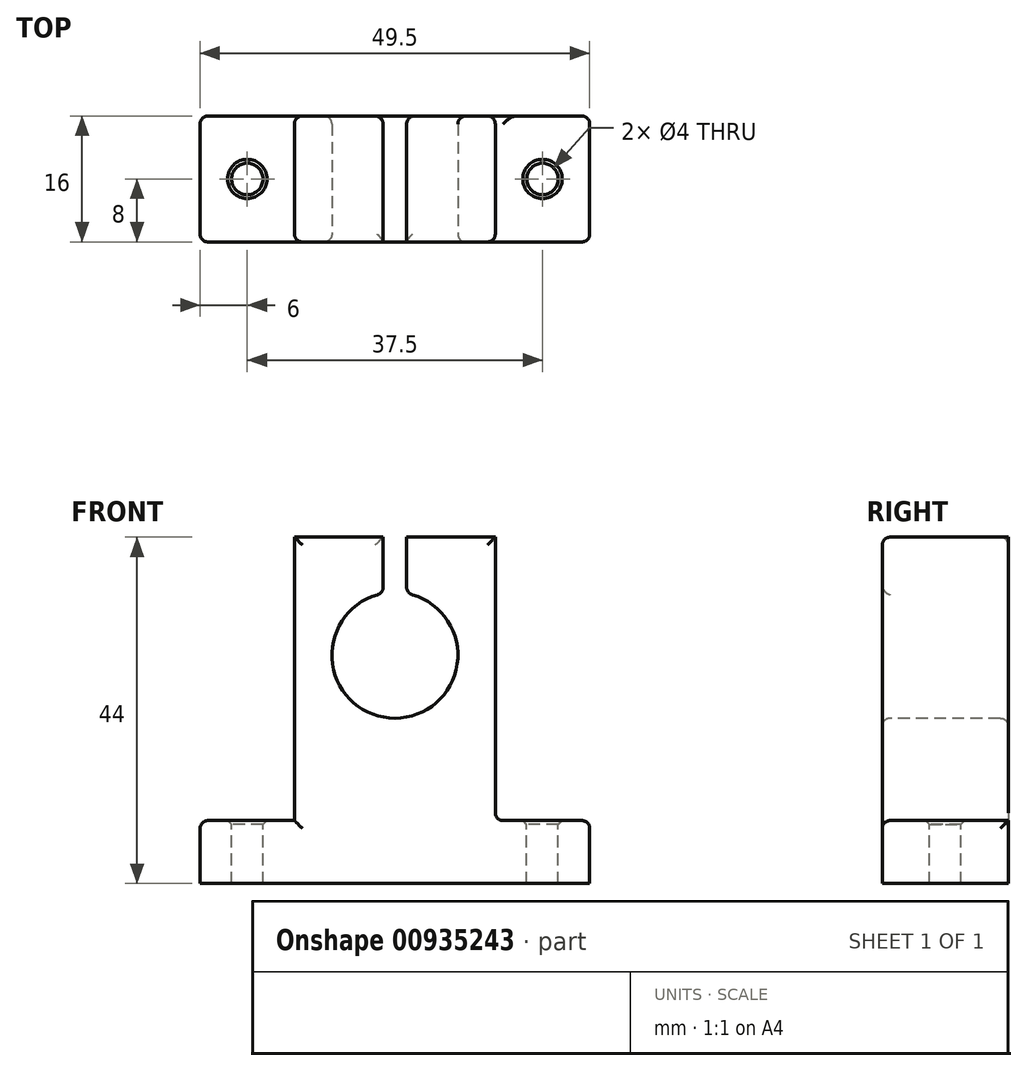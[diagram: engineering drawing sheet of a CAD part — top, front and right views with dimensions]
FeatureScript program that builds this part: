
annotation { "Feature Type Name" : "Feature", "Feature Type Description" : "" }
export const myFeature = defineFeature(function(context is Context, id is Id, definition is map)
    precondition{}
    {
        {
            var Q0;
            Q0=qCreatedBy(makeId("Front.planeOp"),FACE);
            var sketch = newSketch(context, id + "F0", { "sketchPlane" : qUnion([Q0])});
            skLineSegment(sketch, "E0", {"start": v(24.75, -5.32) * mm, "end": v(-24.75, -5.32) * mm});
            skLineSegment(sketch, "E1", {"start": v(-24.75, -5.32) * mm, "end": v(-24.75, 2.68) * mm});
            skLineSegment(sketch, "E2", {"start": v(-24.75, 2.68) * mm, "end": v(-12.75, 2.68) * mm});
            skLineSegment(sketch, "E3", {"start": v(-12.75, 2.68) * mm, "end": v(-12.75, 38.68) * mm});
            skLineSegment(sketch, "E4", {"start": v(-12.75, 38.68) * mm, "end": v(-1.5, 38.68) * mm});
            skLineSegment(sketch, "E5", {"start": v(12.75, 38.68) * mm, "end": v(12.75, 2.68) * mm});
            skLineSegment(sketch, "E6", {"start": v(12.75, 2.68) * mm, "end": v(24.75, 2.68) * mm});
            skLineSegment(sketch, "E7", {"start": v(24.75, 2.68) * mm, "end": v(24.75, -5.32) * mm});
            skLineSegment(sketch, "E8", {"start": v(0, -15.74) * mm, "end": v(0, 30.55) * mm});
            skArc(sketch, "E9", {"start": v(-1.5, 31.54) * mm, "mid": v(0, 15.68) * mm, "end": v(1.5, 31.54) * mm});
            skLineSegment(sketch, "E10", {"start": v(-1.5, 38.68) * mm, "end": v(-1.5, 31.54) * mm});
            skLineSegment(sketch, "E11", {"start": v(1.5, 38.68) * mm, "end": v(1.5, 31.54) * mm});
            skLineSegment(sketch, "E12.trimOffspring", {"start": v(1.5, 38.68) * mm, "end": v(12.75, 38.68) * mm});
            skSolve(sketch);
        }
        {
            var Q0;
            Q0 = qSketchRegion(id + "F0", true);
            extrude(context, id + "F1", {"entities" : qUnion([Q0]), "endBound" : BoundingType.SYMMETRIC, "oppositeDirection" : true, "depth" : 16 * mm, "offsetDistance" : 25 * mm});
        }
        {
            var Q0;
            Q0=makeQuery(id+"F1.opExtrude","SWEPT_FACE",FACE,{"disambiguationData":[OSD([sQuery(id+"F0.wireOp",EDGE,"E6")])]});
            var sketch = newSketch(context, id + "F2", { "sketchPlane" : qUnion([Q0])});
            skPoint(sketch, "E13.centerSnap0", {"position": v(18.75, 8) * mm});
            skPoint(sketch, "E14", {"position": v(18.75, 0) * mm});
            skLineSegment(sketch, "E15", {"start": v(0, 10.96) * mm, "end": v(0, -10.86) * mm, "construction": true});
            skPoint(sketch, "E16.MirrorP", {"position": v(-18.75, 0) * mm});
            skSolve(sketch);
        }
        {
            var Q0;
            Q0=sQuery(id+"F2.wireOp",VERTEX,"E14");
            var Q1;
            Q1=sQuery(id+"F2.wireOp",VERTEX,"E16.MirrorP");
            var Q2;
            Q2=makeQuery(id+"F1.opExtrude","SWEPT_BODY",BODY,{"disambiguationData":[OSD([sQuery(id+"F0.wireOp",EDGE,"E0"),sQuery(id+"F0.wireOp",EDGE,"E1"),sQuery(id+"F0.wireOp",EDGE,"E2"),sQuery(id+"F0.wireOp",EDGE,"E3"),sQuery(id+"F0.wireOp",EDGE,"E4"),sQuery(id+"F0.wireOp",EDGE,"E5"),sQuery(id+"F0.wireOp",EDGE,"E6"),sQuery(id+"F0.wireOp",EDGE,"E7"),sQuery(id+"F0.wireOp",EDGE,"E9"),sQuery(id+"F0.wireOp",EDGE,"E10"),sQuery(id+"F0.wireOp",EDGE,"E11"),sQuery(id+"F0.wireOp",EDGE,"E12.trimOffspring")])]});
            hole(context, id + "F3", {"style" : HoleStyle.C_SINK, "endStyle" : HoleEndStyle.THROUGH, "holeDiameter" : 4 * mm, "cSinkDiameter" : 5 * mm, "cSinkAngle" : 90 * degree, "majorDiameter" : 5 * mm, "isTappedThrough" : true, "tappedDepth" : 12 * mm, "tapClearance" : 3, "locations" : qUnion([Q0, Q1]), "scope" : qUnion([Q2])});
        }
        {
            var Q0;
            Q0=makeQuery(id+"F1.opExtrude","CAP_EDGE",EDGE,{"disambiguationData":[OSD([sQuery(id+"F0.wireOp",EDGE,"E3")])],"isStart":true});
            var Q1;
            Q1=makeQuery(id+"F1.opExtrude","CAP_EDGE",EDGE,{"disambiguationData":[OSD([sQuery(id+"F0.wireOp",EDGE,"E4")])],"isStart":true});
            var Q2;
            Q2=makeQuery(id+"F1.opExtrude","CAP_EDGE",EDGE,{"disambiguationData":[OSD([sQuery(id+"F0.wireOp",EDGE,"E12.trimOffspring")])],"isStart":true});
            var Q3;
            Q3=makeQuery(id+"F1.opExtrude","CAP_EDGE",EDGE,{"disambiguationData":[OSD([sQuery(id+"F0.wireOp",EDGE,"E5")])],"isStart":true});
            var Q4;
            Q4=makeQuery(id+"F1.opExtrude","CAP_EDGE",EDGE,{"disambiguationData":[OSD([sQuery(id+"F0.wireOp",EDGE,"E6")])],"isStart":true});
            var Q5;
            Q5=makeQuery(id+"F1.opExtrude","CAP_EDGE",EDGE,{"disambiguationData":[OSD([sQuery(id+"F0.wireOp",EDGE,"E2")])],"isStart":true});
            var Q6;
            Q6=makeQuery(id+"F1.opExtrude","CAP_EDGE",EDGE,{"disambiguationData":[OSD([sQuery(id+"F0.wireOp",EDGE,"E7")])],"isStart":true});
            var Q7;
            Q7=makeQuery(id+"F1.opExtrude","CAP_EDGE",EDGE,{"disambiguationData":[OSD([sQuery(id+"F0.wireOp",EDGE,"E1")])],"isStart":true});
            var Q8;
            Q8=makeQuery(id+"F1.opExtrude","SWEPT_EDGE",EDGE,{"disambiguationData":[OSD([sQuery(id+"F0.wireOp",EDGE,"E5"),sQuery(id+"F0.wireOp",EDGE,"E6")])]});
            var Q9;
            Q9=makeQuery(id+"F1.opExtrude","SWEPT_EDGE",EDGE,{"disambiguationData":[OSD([sQuery(id+"F0.wireOp",EDGE,"E6"),sQuery(id+"F0.wireOp",EDGE,"E7")])]});
            var Q10;
            Q10=makeQuery(id+"F1.opExtrude","CAP_EDGE",EDGE,{"disambiguationData":[OSD([sQuery(id+"F0.wireOp",EDGE,"E7")])],"isStart":false});
            var Q11;
            Q11=makeQuery(id+"F1.opExtrude","CAP_EDGE",EDGE,{"disambiguationData":[OSD([sQuery(id+"F0.wireOp",EDGE,"E5")])],"isStart":false});
            var Q12;
            Q12=makeQuery(id+"F1.opExtrude","CAP_EDGE",EDGE,{"disambiguationData":[OSD([sQuery(id+"F0.wireOp",EDGE,"E11")])],"isStart":false});
            var Q13;
            Q13=makeQuery(id+"F1.opExtrude","CAP_EDGE",EDGE,{"disambiguationData":[OSD([sQuery(id+"F0.wireOp",EDGE,"E10")])],"isStart":false});
            var Q14;
            Q14=makeQuery(id+"F1.opExtrude","SWEPT_FACE",FACE,{"disambiguationData":[OSD([sQuery(id+"F0.wireOp",EDGE,"E9")])]});
            var Q15;
            Q15=makeQuery(id+"F1.opExtrude","CAP_EDGE",EDGE,{"disambiguationData":[OSD([sQuery(id+"F0.wireOp",EDGE,"E4")])],"isStart":false});
            var Q16;
            Q16=makeQuery(id+"F1.opExtrude","CAP_EDGE",EDGE,{"disambiguationData":[OSD([sQuery(id+"F0.wireOp",EDGE,"E3")])],"isStart":false});
            var Q17;
            Q17=makeQuery(id+"F1.opExtrude","CAP_EDGE",EDGE,{"disambiguationData":[OSD([sQuery(id+"F0.wireOp",EDGE,"E2")])],"isStart":false});
            var Q18;
            Q18=makeQuery(id+"F1.opExtrude","CAP_EDGE",EDGE,{"disambiguationData":[OSD([sQuery(id+"F0.wireOp",EDGE,"E1")])],"isStart":false});
            var Q19;
            Q19=makeQuery(id+"F1.opExtrude","SWEPT_EDGE",EDGE,{"disambiguationData":[OSD([sQuery(id+"F0.wireOp",EDGE,"E1"),sQuery(id+"F0.wireOp",EDGE,"E2")])]});
            fillet(context, id + "F4", {"entities" : qUnion([Q0, Q1, Q2, Q3, Q4, Q5, Q6, Q7, Q8, Q9, Q10, Q11, Q12, Q13, Q14, Q15, Q16, Q17, Q18, Q19]), "radius" : 1 * mm, "tangentPropagation" : true, "allowEdgeOverflow" : false});
        }
    });
